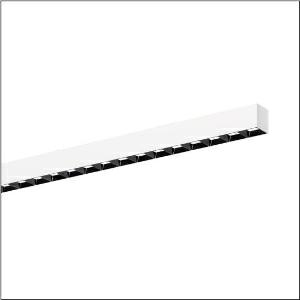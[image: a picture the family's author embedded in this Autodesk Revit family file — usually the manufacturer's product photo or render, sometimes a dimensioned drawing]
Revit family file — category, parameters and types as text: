
# Revit family: silica_r__21_51mx21dc4awb_19b2
name_source: partatom
category: Lighting Fixtures
units: mm (PartAtom-declared; Revit-internal decimal feet)

## family parameters
Cut with Voids When Loaded = No
Host = Face
Light Source = No
Part Type = Normal
Room Calculation Point = No
Round Connector Dimension = Use Diameter
Shared = No

## types (1)
- --- (1 x LED, 10800 lm, 64.8 W, 4000K)
    Apparent Load = 65 VA
    CIE Flux Codes = 87 99 100 100 100
    Color Rendering = 80
    Color Temperature = 4000K
    Default Elevation = 1800 mm
    Description = Silica® 21, office luminaire, primary light control with darklight reflector, of PMMA, black, CAT 2 (L<= 3000cd/m²), light emission: direct distribution, primary light characteristic: symmetric, installation type: surface-mounted, LED, rated luminous flux: 10.800lm, luminous efficacy: 167lm/W, light colour: 840, colour temperature: 4000K, with terminal, 3+2-pole, max. 2.5mm², mains connection: 220..240V, AC, 50/60Hz, rated input power: 64.8W, luminaire housing, of aluminium, traffic white (RAL 9016), length: 3.004mm, width: 53mm, height: 53mm, protection rating (complete): IP20, insulation class (complete): insulation class I (protective earthing), certification: CE, permissible operating ambient temperature: 0..+35°C, standard: EN 50419, packaging unit: 1 piece
    Height = 0 mm  [stored 0 ft]
    Lamp = 1 x LED
    Lamp Light Flux = 10800 lm
    Lamp Power = 64.8 W
    Lamp count = 1
    Length = 3004 mm
    Luminous efficacy = 167 lm/W
    Manufacturer = Siteco
    ModVariant = No
    Model = 51MX21DC4AWB
    Mounting Place = Ceiling
    Mounting Type = Recessed
    Number of Poles = 1
    OnlyDefault = Yes
    Power Factor = 1
    Product Name = Silica® 21
    Product group = office luminaire | ceiling recessed
    ProductGroupID = 401
    Protection Class = Protection class I
    Protection Degree = IP 20
    RLX_Detail_Level = 1
    RLX_Emergency_Light_Flux = 0 lm
    RLX_Emergency_Type = 0
    RLX_Emergency_Type_DB = No
    RlxData = <blob elided: 61089 chars, md5=35e75586>
    Socket = socket
    Standby Power = 0 W
    System Light Flux = 10800 lm
    System Power = 65 W
    Type Comments = factory setting: luminous flux: 100 % | dim-lin: 254 | 367 mA
    Type Image = l_1297779.jpg
    URL = http://relux.com
    VarID = @adj_054821
    Voltage = 0 V
    Weight = 0.00 kg
    Width = 53 mm

note: [stored X ft] marks values corroborated as IEEE doubles in the binary element streams (Revit-internal decimal feet)

## geometry (parser evidence)
native form markers: Blend x4, Sweep x11
no freeform markers — native parametric forms only
